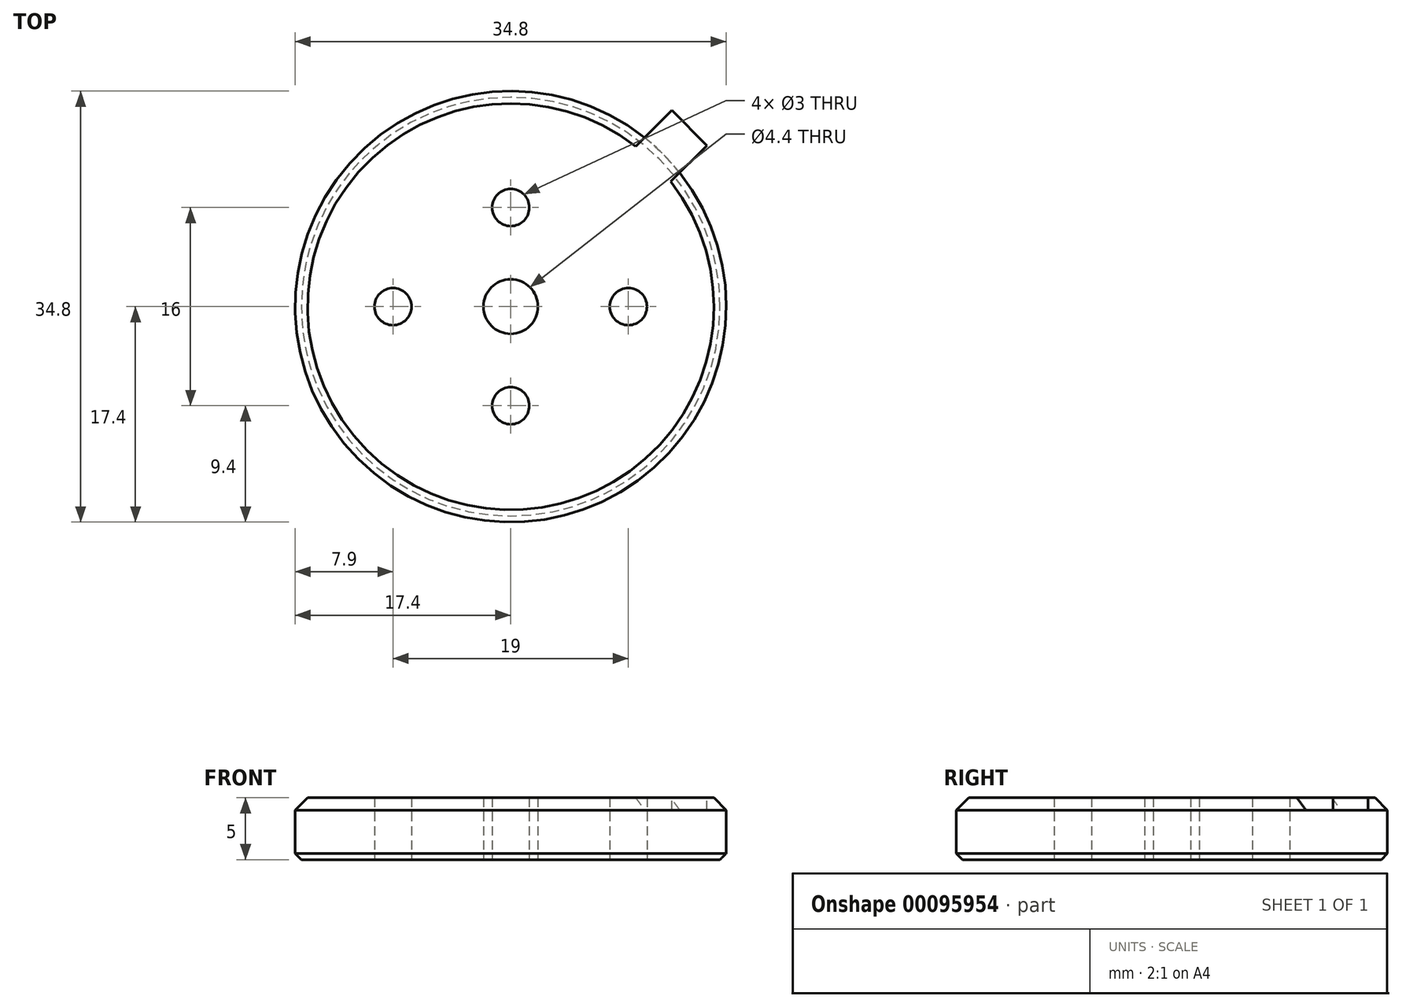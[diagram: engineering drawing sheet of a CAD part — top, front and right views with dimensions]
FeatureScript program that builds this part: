
annotation { "Feature Type Name" : "Feature", "Feature Type Description" : "" }
export const myFeature = defineFeature(function(context is Context, id is Id, definition is map)
    precondition{}
    {
        {
            var Q0;
            Q0=qCreatedBy(makeId("Top.planeOp"),FACE);
            var sketch = newSketch(context, id + "F0", { "sketchPlane" : qUnion([Q0])});
            skCircle(sketch, "E0", {"center": v(0, 0) * mm, "radius": 17.4 * mm});
            skCircle(sketch, "E1", {"center": v(0, 0) * mm, "radius": 2.2 * mm});
            skCircle(sketch, "E2", {"center": v(0, 8) * mm, "radius": 1.5 * mm});
            skCircle(sketch, "E3.1.0", {"center": v(-9.5, 0) * mm, "radius": 1.5 * mm});
            skCircle(sketch, "E3.2.0", {"center": v(0, -8) * mm, "radius": 1.5 * mm});
            skCircle(sketch, "E3.3.0", {"center": v(9.5, 0) * mm, "radius": 1.5 * mm});
            skSolve(sketch);
        }
        {
            var Q0;
            Q0=qSketchRegion(id+"F0",true);
            extrude(context, id + "F1", {"entities" : qUnion([Q0]), "depth" : 5 * mm});
        }
        {
            var Q0;
            Q0=makeQuery(id+"F1.opExtrude","CAP_EDGE",EDGE,{"disambiguationData":[OSD([sQuery(id+"F0.wireOp",EDGE,"E0")])],"isStart":false});
            chamfer(context, id + "F2", {"entities" : qUnion([Q0]), "width" : 1 * mm, "tangentPropagation" : true});
        }
        {
            var Q0;
            Q0=makeQuery(id+"F1.opExtrude","CAP_EDGE",EDGE,{"disambiguationData":[OSD([sQuery(id+"F0.wireOp",EDGE,"E0")])],"isStart":true});
            chamfer(context, id + "F3", {"entities" : qUnion([Q0]), "width" : .5 * mm, "tangentPropagation" : true});
        }
        {
            var Q0;
            Q0=makeQuery(id+"F1.opExtrude","CAP_FACE",FACE,{"disambiguationData":[OSD([sQuery(id+"F0.wireOp",EDGE,"E0"),sQuery(id+"F0.wireOp",EDGE,"E1"),sQuery(id+"F0.wireOp",EDGE,"E2"),sQuery(id+"F0.wireOp",EDGE,"E3.1.0"),sQuery(id+"F0.wireOp",EDGE,"E3.2.0"),sQuery(id+"F0.wireOp",EDGE,"E3.3.0")])],"isStart":false});
            var sketch = newSketch(context, id + "F4", { "sketchPlane" : qUnion([Q0])});
            skLineSegment(sketch, "E4", {"start": v(0, 24.6) * mm, "end": v(24.6, 0) * mm, "construction": true});
            skLineSegment(sketch, "E5", {"start": v(0, 24.6) * mm, "end": v(0, 0) * mm, "construction": true});
            skLineSegment(sketch, "E6", {"start": v(0, 0) * mm, "end": v(24.6, 0) * mm, "construction": true});
            skPoint(sketch, "E7", {"position": v(12.3, 12.3) * mm});
            skLineSegment(sketch, "E8", {"start": v(9.83, 12.66) * mm, "end": v(13.01, 15.84) * mm});
            skLineSegment(sketch, "E9", {"start": v(13.01, 15.84) * mm, "end": v(15.84, 13.01) * mm});
            skLineSegment(sketch, "E10", {"start": v(15.84, 13.01) * mm, "end": v(12.66, 9.83) * mm});
            skLineSegment(sketch, "E11", {"start": v(12.66, 9.83) * mm, "end": v(9.83, 12.66) * mm});
            skSolve(sketch);
        }
        {
            var Q0;
            Q0 = qSketchRegion(id + "F4", true);
            extrude(context, id + "F5", {"entities" : qUnion([Q0]), "operationType" : NewBodyOperationType.ADD, "oppositeDirection" : true, "depth" : 1 * mm});
        }
    });
